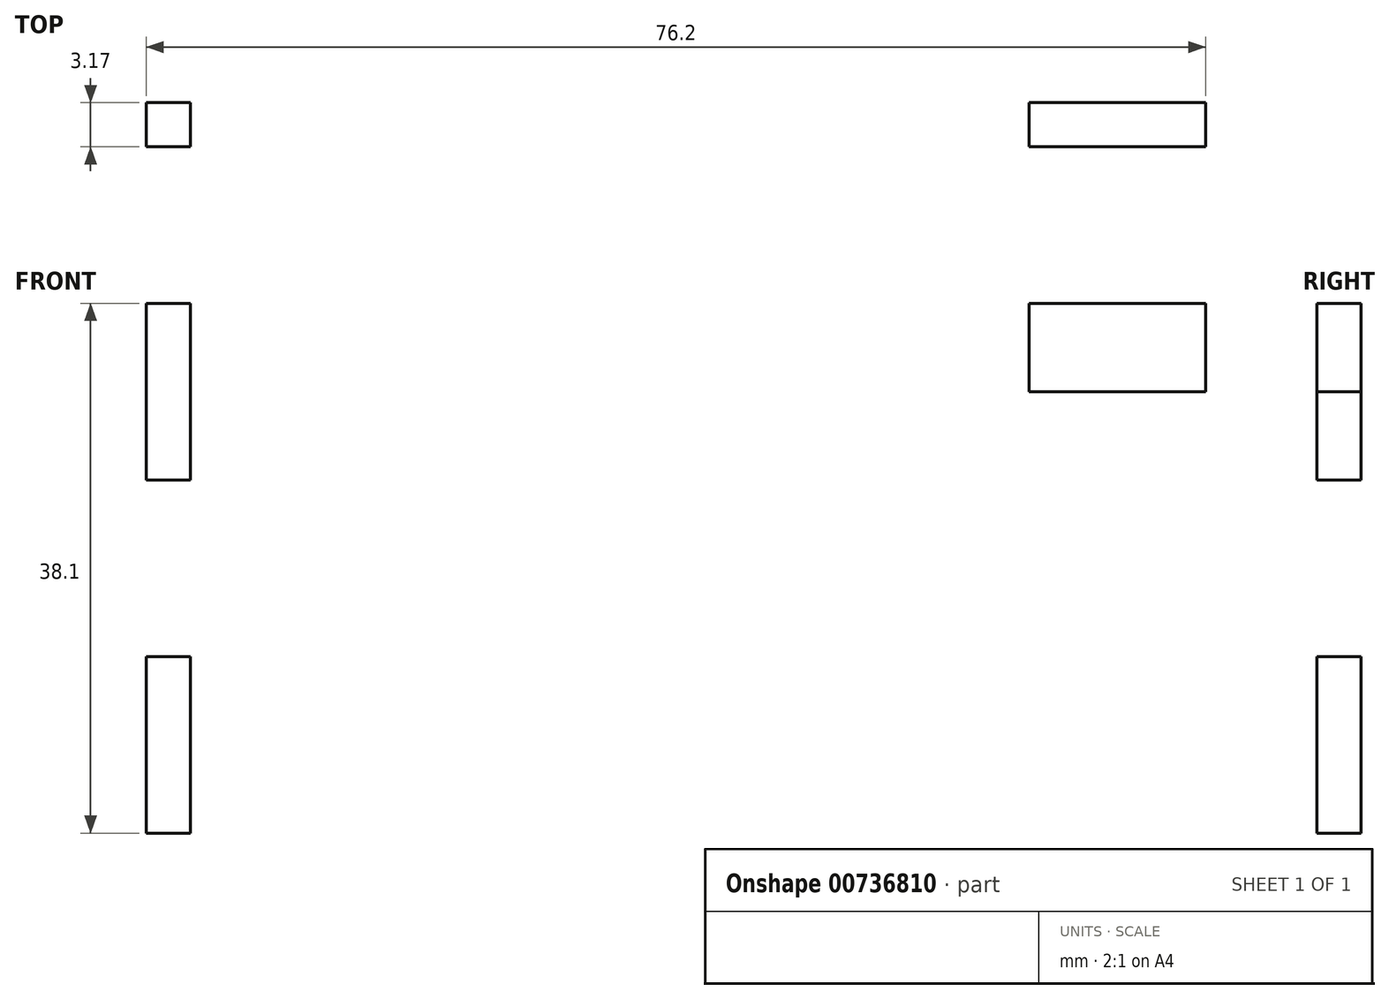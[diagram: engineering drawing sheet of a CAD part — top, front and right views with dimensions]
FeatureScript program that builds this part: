
annotation { "Feature Type Name" : "Feature", "Feature Type Description" : "" }
export const myFeature = defineFeature(function(context is Context, id is Id, definition is map)
    precondition{}
    {
        {
            var Q0;
            Q0=qCreatedBy(makeId("Front.planeOp"),FACE);
            var sketch = newSketch(context, id + "F0", { "sketchPlane" : qUnion([Q0])});
            skLineSegment(sketch, "E0.bottom", {"start": v(0, 0) * mm, "end": v(-127, 0) * mm});
            skLineSegment(sketch, "E0.top", {"start": v(0, 38.1) * mm, "end": v(-127, 38.1) * mm});
            skLineSegment(sketch, "E0.left", {"start": v(0, 0) * mm, "end": v(0, 38.1) * mm});
            skLineSegment(sketch, "E0.right", {"start": v(-127, 0) * mm, "end": v(-127, 38.1) * mm});
            skLineSegment(sketch, "E1.bottom", {"start": v(-127, 0) * mm, "end": v(-123.82, 0) * mm});
            skLineSegment(sketch, "E1.top", {"start": v(-127, 12.7) * mm, "end": v(-123.82, 12.7) * mm});
            skLineSegment(sketch, "E1.left", {"start": v(-127, 0) * mm, "end": v(-127, 12.7) * mm});
            skLineSegment(sketch, "E1.right", {"start": v(-123.82, 0) * mm, "end": v(-123.82, 12.7) * mm});
            skLineSegment(sketch, "E2.bottom", {"start": v(-127, 38.1) * mm, "end": v(-123.82, 38.1) * mm});
            skLineSegment(sketch, "E2.top", {"start": v(-127, 25.4) * mm, "end": v(-123.82, 25.4) * mm});
            skLineSegment(sketch, "E2.left", {"start": v(-127, 38.1) * mm, "end": v(-127, 25.4) * mm});
            skLineSegment(sketch, "E2.right", {"start": v(-123.82, 38.1) * mm, "end": v(-123.82, 25.4) * mm});
            skLineSegment(sketch, "E3", {"start": v(-63.5, 0) * mm, "end": v(-63.5, 38.1) * mm});
            skLineSegment(sketch, "E4.MirrorCS", {"start": v(-3.17, 38.1) * mm, "end": v(-3.17, 25.4) * mm});
            skLineSegment(sketch, "E5.MirrorCS", {"start": v(0, 25.4) * mm, "end": v(-3.17, 25.4) * mm});
            skLineSegment(sketch, "E6.MirrorCS", {"start": v(0, 12.7) * mm, "end": v(-3.17, 12.7) * mm});
            skLineSegment(sketch, "E7.MirrorCS", {"start": v(-3.17, 0) * mm, "end": v(-3.17, 12.7) * mm});
            skLineSegment(sketch, "E8.bottom", {"start": v(-63.5, 38.1) * mm, "end": v(-76.2, 38.1) * mm});
            skLineSegment(sketch, "E8.top", {"start": v(-63.5, 31.75) * mm, "end": v(-76.2, 31.75) * mm});
            skLineSegment(sketch, "E8.left", {"start": v(-63.5, 38.1) * mm, "end": v(-63.5, 31.75) * mm});
            skLineSegment(sketch, "E8.right", {"start": v(-76.2, 38.1) * mm, "end": v(-76.2, 31.75) * mm});
            skLineSegment(sketch, "E9.MirrorCS", {"start": v(-63.5, 31.75) * mm, "end": v(-50.8, 31.75) * mm});
            skLineSegment(sketch, "E10.MirrorCS", {"start": v(-50.8, 38.1) * mm, "end": v(-50.8, 31.75) * mm});
            skSolve(sketch);
        }
        {
            var Q0;
            Q0=makeQuery(id+"F0.imprint","IMPRINT",FACE,{"disambiguationData":[TD([[makeQuery(id+"F0.imprint","IMPRINT",EDGE,{"derivedFrom":sQuery(id+"F0.wireOp",EDGE,"E0.right")}),-1.0]])]});
            var Q1;
            {var subQ3=sQuery(id+"F0.wireOp",EDGE,"E3");Q1=makeQuery(id+"F0.imprint","IMPRINT",FACE,{"disambiguationData":[TD([[makeQuery(id+"F0.imprint","IMPRINT",EDGE,{"derivedFrom":subQ3}),-1.0]])]});}
            extrude(context, id + "F1", {"entities" : qUnion([Q0, Q1]), "depth" : 3.17 * mm, "offsetDistance" : 25.4 * mm});
        }
    });
